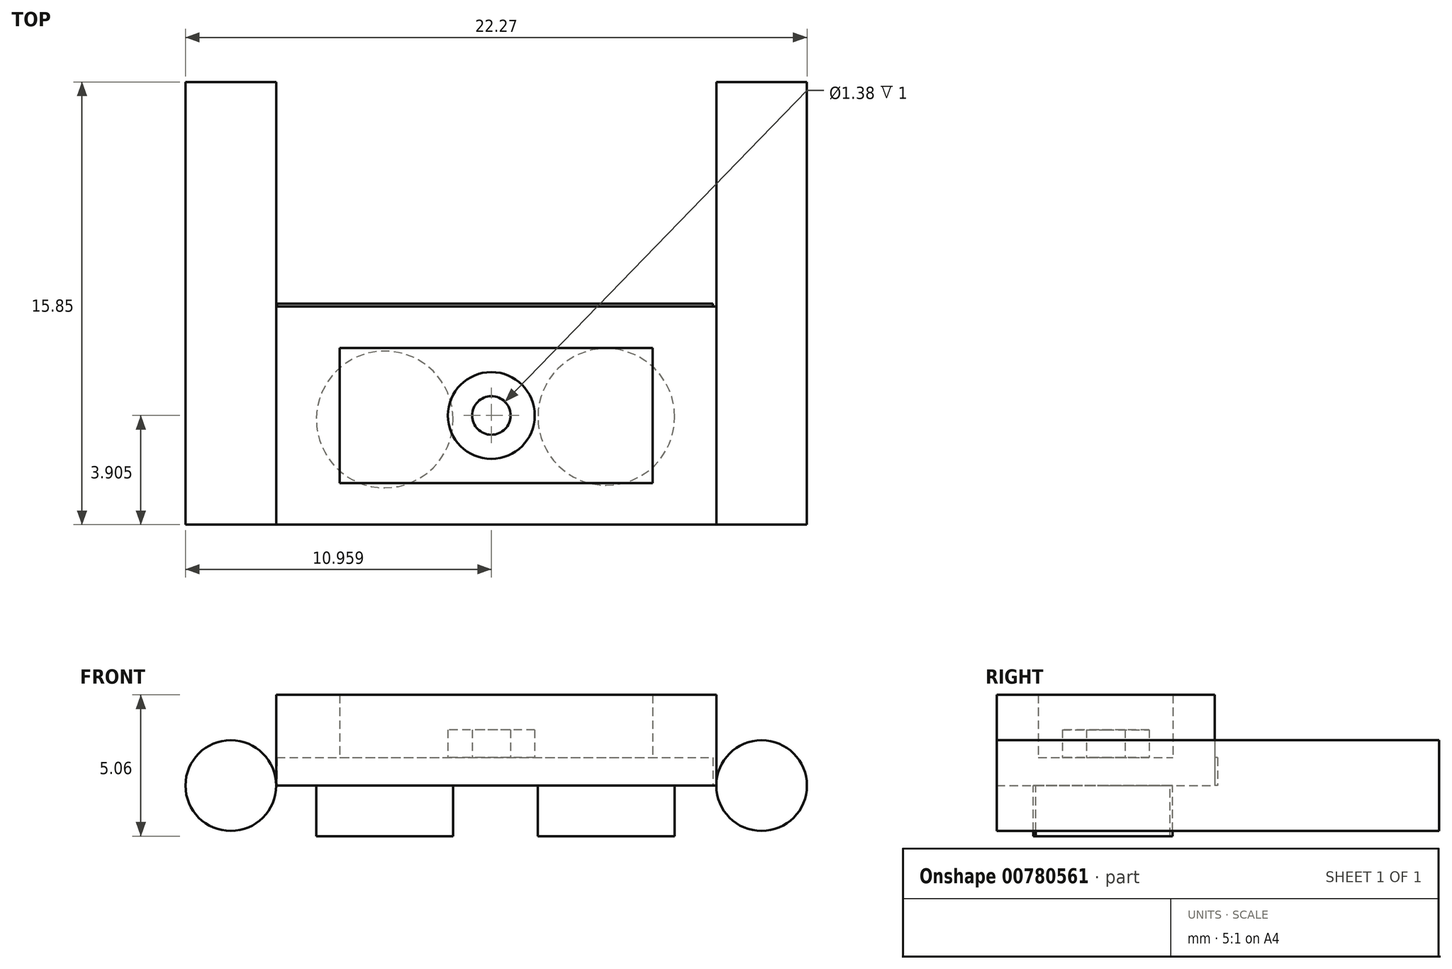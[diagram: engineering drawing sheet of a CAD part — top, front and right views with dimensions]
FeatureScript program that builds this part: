
annotation { "Feature Type Name" : "Feature", "Feature Type Description" : "" }
export const myFeature = defineFeature(function(context is Context, id is Id, definition is map)
    precondition{}
    {
        {
            var Q0;
            Q0=qCreatedBy(makeId("Top.planeOp"),FACE);
            var sketch = newSketch(context, id + "F0", { "sketchPlane" : qUnion([Q0])});
            skLineSegment(sketch, "E0.bottom", {"start": v(-18.07, 0) * mm, "end": v(-2.3, 0) * mm});
            skLineSegment(sketch, "E0.top", {"start": v(-18.07, 7.81) * mm, "end": v(-2.3, 7.81) * mm});
            skLineSegment(sketch, "E0.left", {"start": v(-18.07, 0) * mm, "end": v(-18.07, 7.81) * mm});
            skLineSegment(sketch, "E0.right", {"start": v(-2.3, 0) * mm, "end": v(-2.3, 7.8) * mm});
            skSolve(sketch);
        }
        {
            var Q0;
            Q0 = qSketchRegion(id + "F0", true);
            extrude(context, id + "F1", {"entities" : qUnion([Q0]), "depth" : 3.25 * mm, "offsetDistance" : 25 * mm});
        }
        {
            var Q0;
            Q0=qCreatedBy(makeId("Front.planeOp"),FACE);
            var sketch = newSketch(context, id + "F2", { "sketchPlane" : qUnion([Q0])});
            skCircle(sketch, "E1", {"center": v(-19.7, 0) * mm, "radius": 1.63 * mm});
            skPoint(sketch, "E2.center.orphan", {"position": v(0, 0) * mm});
            skCircle(sketch, "E3", {"center": v(-0.68, 0) * mm, "radius": 1.63 * mm});
            skSolve(sketch);
        }
        {
            var Q0;
            Q0 = qSketchRegion(id + "F2", true);
            extrude(context, id + "F3", {"entities" : qUnion([Q0]), "oppositeDirection" : true, "depth" : 15.85 * mm, "offsetDistance" : 25 * mm});
        }
        {
            var Q0;
            Q0=qCreatedBy(makeId("Top.planeOp"),FACE);
            var sketch = newSketch(context, id + "F4", { "sketchPlane" : qUnion([Q0])});
            skLineSegment(sketch, "E4.bottom", {"start": v(-15.8, 1.49) * mm, "end": v(-4.58, 1.49) * mm});
            skLineSegment(sketch, "E4.top", {"start": v(-15.8, 6.32) * mm, "end": v(-4.58, 6.32) * mm});
            skLineSegment(sketch, "E4.left", {"start": v(-15.8, 1.49) * mm, "end": v(-15.8, 6.32) * mm});
            skLineSegment(sketch, "E4.right", {"start": v(-4.58, 1.49) * mm, "end": v(-4.58, 6.32) * mm});
            skSolve(sketch);
        }
        {
            var Q0;
            Q0 = qSketchRegion(id + "F4", true);
            extrude(context, id + "F5", {"entities" : qUnion([Q0]), "operationType" : NewBodyOperationType.REMOVE, "depth" : 25 * mm, "offsetDistance" : 25 * mm});
        }
        {
            var Q0;
            Q0=qCreatedBy(makeId("Top.planeOp"),FACE);
            var sketch = newSketch(context, id + "F6", { "sketchPlane" : qUnion([Q0])});
            skLineSegment(sketch, "E5.bottom", {"start": v(-18.05, 7.91) * mm, "end": v(-2.42, 7.91) * mm});
            skLineSegment(sketch, "E5.top", {"start": v(-18.05, 0) * mm, "end": v(-2.42, 0) * mm});
            skLineSegment(sketch, "E5.left", {"start": v(-18.05, 7.91) * mm, "end": v(-18.05, 0) * mm});
            skLineSegment(sketch, "E5.right", {"start": v(-2.42, 7.91) * mm, "end": v(-2.42, 0) * mm});
            skSolve(sketch);
        }
        {
            var Q0;
            Q0 = qSketchRegion(id + "F6", true);
            extrude(context, id + "F7", {"entities" : qUnion([Q0]), "operationType" : NewBodyOperationType.ADD, "depth" : 1 * mm, "offsetDistance" : 25 * mm});
        }
        {
            var Q0;
            Q0=qCreatedBy(makeId("Top.planeOp"),FACE);
            var sketch = newSketch(context, id + "F8", { "sketchPlane" : qUnion([Q0])});
            skCircle(sketch, "E6", {"center": v(-14.18, 3.76) * mm, "radius": 2.45 * mm});
            skCircle(sketch, "E7", {"center": v(-6.24, 3.85) * mm, "radius": 2.45 * mm});
            skSolve(sketch);
        }
        {
            var Q0;
            Q0 = qSketchRegion(id + "F8", true);
            extrude(context, id + "F9", {"entities" : qUnion([Q0]), "operationType" : NewBodyOperationType.ADD, "oppositeDirection" : true, "depth" : 1.81 * mm, "offsetDistance" : 25 * mm});
        }
        {
            var Q0;
            Q0=qCreatedBy(makeId("Top.planeOp"),FACE);
            var sketch = newSketch(context, id + "F10", { "sketchPlane" : qUnion([Q0])});
            skCircle(sketch, "E8", {"center": v(-10.36, 3.9) * mm, "radius": 1.55 * mm});
            skCircle(sketch, "E9", {"center": v(-10.36, 3.9) * mm, "radius": 0.69 * mm});
            skSolve(sketch);
        }
        {
            var Q0;
            Q0 = qSketchRegion(id + "F10", true);
            extrude(context, id + "F11", {"entities" : qUnion([Q0]), "operationType" : NewBodyOperationType.ADD, "depth" : 2 * mm, "offsetDistance" : 25 * mm});
        }
    });
